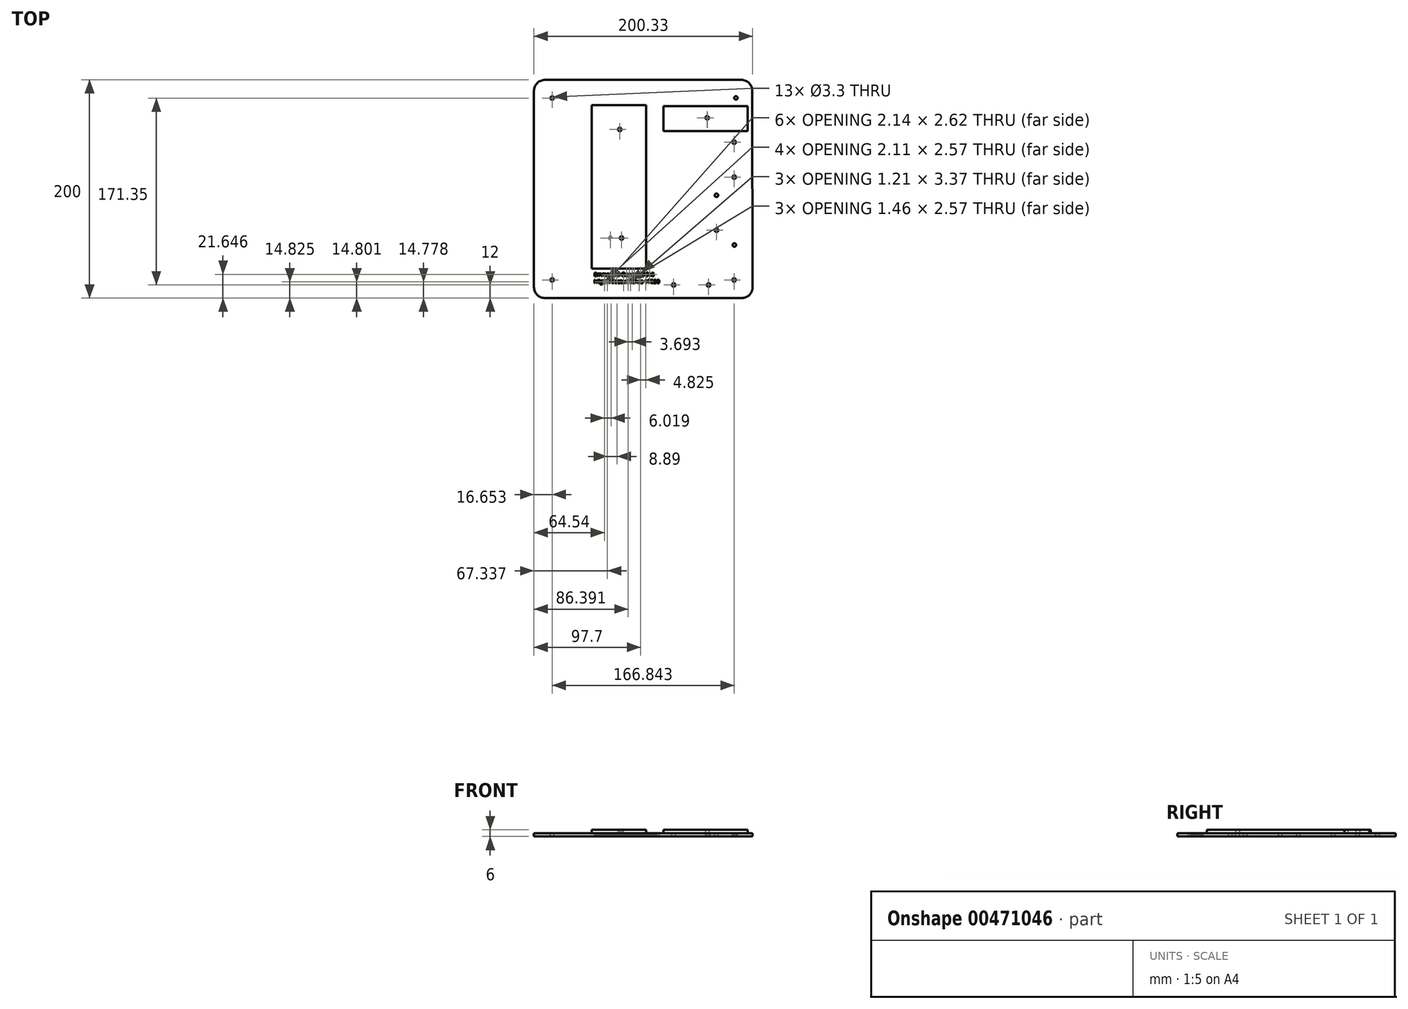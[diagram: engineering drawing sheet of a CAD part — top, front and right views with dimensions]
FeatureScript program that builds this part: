
annotation { "Feature Type Name" : "Feature", "Feature Type Description" : "" }
export const myFeature = defineFeature(function(context is Context, id is Id, definition is map)
    precondition{}
    {
        {
            var Q0;
            Q0=qCreatedBy(makeId("Top.planeOp"),FACE);
            var sketch = newSketch(context, id + "F0", { "sketchPlane" : qUnion([Q0])});
            skLineSegment(sketch, "E0", {"start": v(-96.19, 218.28) * mm, "end": v(83.81, 218.28) * mm});
            skLineSegment(sketch, "E1", {"start": v(-106.19, 208.28) * mm, "end": v(-106.19, 28.28) * mm});
            skLineSegment(sketch, "E2", {"start": v(-96.19, 18.28) * mm, "end": v(84.14, 18.28) * mm});
            skLineSegment(sketch, "E3", {"start": v(93.81, 208.3) * mm, "end": v(94.14, 28.3) * mm});
            skPoint(sketch, "E4.visualSharp", {"position": v(-106.19, 218.28) * mm});
            skArc(sketch, "E4.filletArc", {"start": v(-96.19, 218.28) * mm, "mid": v(-103.26, 215.35) * mm, "end": v(-106.19, 208.28) * mm});
            skPoint(sketch, "E5.visualSharp", {"position": v(93.8, 218.28) * mm});
            skArc(sketch, "E5.filletArc", {"start": v(93.81, 208.3) * mm, "mid": v(90.88, 215.36) * mm, "end": v(83.81, 218.28) * mm});
            skPoint(sketch, "E6.visualSharp", {"position": v(94.16, 18.28) * mm});
            skArc(sketch, "E6.filletArc", {"start": v(84.14, 18.28) * mm, "mid": v(91.22, 21.22) * mm, "end": v(94.14, 28.3) * mm});
            skPoint(sketch, "E7.visualSharp", {"position": v(-106.19, 18.28) * mm});
            skArc(sketch, "E7.filletArc", {"start": v(-106.19, 28.28) * mm, "mid": v(-103.26, 21.2) * mm, "end": v(-96.19, 18.28) * mm});
            skCircle(sketch, "E8", {"center": v(-89.54, 34.93) * mm, "radius": 1.65 * mm});
            skCircle(sketch, "E9", {"center": v(77.16, 34.93) * mm, "radius": 1.65 * mm});
            skCircle(sketch, "E10", {"center": v(78.83, 201.71) * mm, "radius": 1.57 * mm});
            skCircle(sketch, "E11", {"center": v(-89.54, 201.63) * mm, "radius": 1.65 * mm});
            skCircle(sketch, "E12", {"center": v(-36.19, 73.28) * mm, "radius": 1.65 * mm});
            skCircle(sketch, "E13", {"center": v(52.67, 183.28) * mm, "radius": 1.65 * mm});
            skText(sketch, "E14", { "text": "Emmanuel Guerra 17615\nMiguel Basterrechea 17350\n", "fontName": "OpenSans-Regular.ttf"});
            skCircle(sketch, "E15", {"center": v(61.04, 80.47) * mm, "radius": 1.65 * mm});
            skCircle(sketch, "E16", {"center": v(77.3, 129.14) * mm, "radius": 1.65 * mm});
            skCircle(sketch, "E17", {"center": v(77.42, 66.93) * mm, "radius": 1.6 * mm});
            skCircle(sketch, "E18", {"center": v(60.99, 112.47) * mm, "radius": 1.6 * mm});
            skCircle(sketch, "E19", {"center": v(77.25, 161.14) * mm, "radius": 1.65 * mm});
            skCircle(sketch, "E20", {"center": v(53.78, 30.28) * mm, "radius": 1.65 * mm});
            skCircle(sketch, "E21", {"center": v(21.78, 30.28) * mm, "radius": 1.65 * mm});
            const initialGuessF0  = {"E14": [-0.05113, 0.03824, 1, 0, 0.0034]};
            skSetInitialGuess(sketch, initialGuessF0);
            skSolve(sketch);
        }
        {
            var Q0;
            Q0=makeQuery(id+"F0.imprint","IMPRINT",FACE,{"disambiguationData":[TD([[makeQuery(id+"F0.imprint","IMPRINT",EDGE,{"derivedFrom":sQuery(id+"F0.wireOp",EDGE,"E0")}),-1.0]])]});
            var sketch = newSketch(context, id + "F1", { "sketchPlane" : qUnion([Q0])});
            skCircle(sketch, "E22", {"center": v(-25.92, 73.28) * mm, "radius": 1.65 * mm});
            skLineSegment(sketch, "E23.bottom", {"start": v(12.55, 171.21) * mm, "end": v(89.55, 171.21) * mm});
            skLineSegment(sketch, "E23.top", {"start": v(12.55, 194.21) * mm, "end": v(89.55, 194.21) * mm});
            skLineSegment(sketch, "E23.left", {"start": v(12.55, 171.21) * mm, "end": v(12.55, 194.21) * mm});
            skLineSegment(sketch, "E23.right", {"start": v(89.55, 171.21) * mm, "end": v(89.55, 194.21) * mm});
            skCircle(sketch, "E24", {"center": v(52.5, 183.48) * mm, "radius": 1.65 * mm});
            skLineSegment(sketch, "E25.bottom", {"start": v(-53.45, 45.28) * mm, "end": v(-3.45, 45.28) * mm});
            skLineSegment(sketch, "E25.top", {"start": v(-53.45, 195.28) * mm, "end": v(-3.45, 195.28) * mm});
            skLineSegment(sketch, "E25.left", {"start": v(-53.45, 45.28) * mm, "end": v(-53.45, 195.28) * mm});
            skLineSegment(sketch, "E25.right", {"start": v(-3.45, 45.28) * mm, "end": v(-3.45, 195.28) * mm});
            skCircle(sketch, "E26", {"center": v(-27.61, 172.8) * mm, "radius": 1.65 * mm});
            skSolve(sketch);
        }
        {
            var Q0;
            Q0 = qSketchRegion(id + "F1", true);
            extrude(context, id + "F2", {"entities" : qUnion([Q0]), "depth" : 3 * mm});
        }
        {
            var Q0;
            Q0 = qSketchRegion(id + "F0", true);
            extrude(context, id + "F3", {"entities" : qUnion([Q0]), "oppositeDirection" : true, "depth" : 3 * mm});
        }
    });
